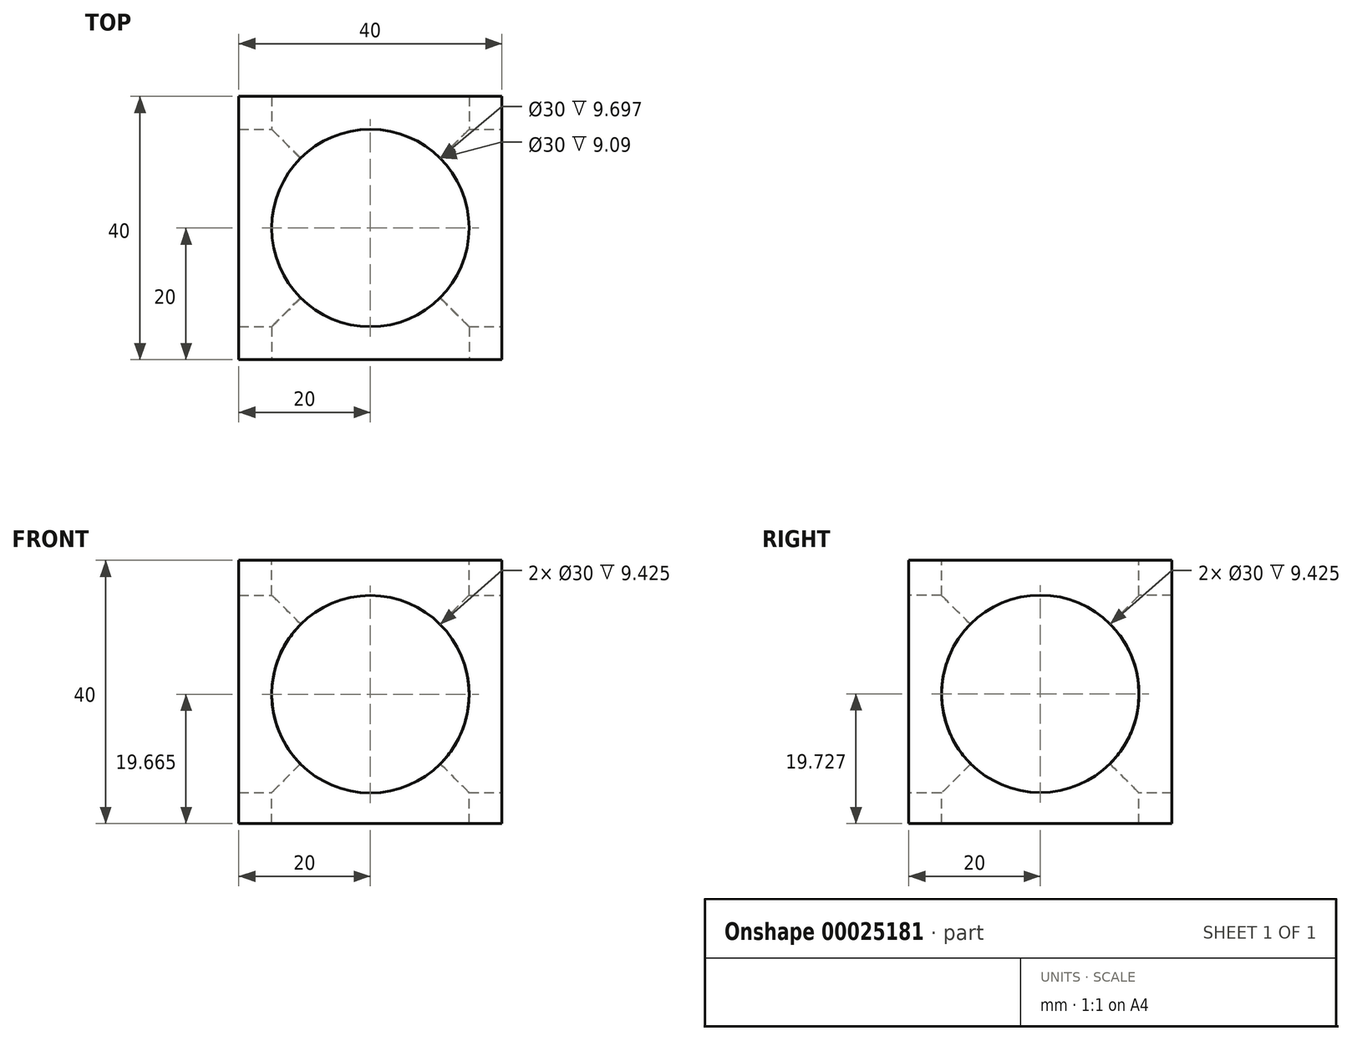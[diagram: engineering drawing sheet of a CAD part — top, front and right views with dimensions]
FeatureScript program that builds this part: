
annotation { "Feature Type Name" : "Feature", "Feature Type Description" : "" }
export const myFeature = defineFeature(function(context is Context, id is Id, definition is map)
    precondition{}
    {
        {
            var Q0;
            Q0=qCreatedBy(makeId("Top.planeOp"),FACE);
            var sketch = newSketch(context, id + "F0", { "sketchPlane" : qUnion([Q0])});
            skLineSegment(sketch, "E0.rect.bottom", {"start": v(20, -20) * mm, "end": v(-20, -20) * mm});
            skLineSegment(sketch, "E0.rect.top", {"start": v(20, 20) * mm, "end": v(-20, 20) * mm});
            skLineSegment(sketch, "E0.rect.left", {"start": v(20, -20) * mm, "end": v(20, 20) * mm});
            skLineSegment(sketch, "E0.rect.right", {"start": v(-20, -20) * mm, "end": v(-20, 20) * mm});
            skPoint(sketch, "E0.rect.middle", {"position": v(0, 0) * mm});
            skSolve(sketch);
        }
        {
            var Q0;
            Q0=makeQuery(id+"F0.imprint","IMPRINT",FACE,{"disambiguationData":[TD([[makeQuery(id+"F0.imprint","IMPRINT",EDGE,{"derivedFrom":sQuery(id+"F0.wireOp",EDGE,"E0.rect.bottom")}),-1.0]])]});
            extrude(context, id + "F1", {"entities" : qUnion([Q0]), "depth" : 40 * mm});
        }
        {
            var Q0;
            Q0=makeQuery(id+"F1.opExtrude","CAP_FACE",FACE,{"disambiguationData":[OSD([sQuery(id+"F0.wireOp",EDGE,"E0.rect.bottom"),sQuery(id+"F0.wireOp",EDGE,"E0.rect.top"),sQuery(id+"F0.wireOp",EDGE,"E0.rect.left"),sQuery(id+"F0.wireOp",EDGE,"E0.rect.right")])],"isStart":false});
            var sketch = newSketch(context, id + "F2", { "sketchPlane" : qUnion([Q0])});
            skCircle(sketch, "E1", {"center": v(0, 0) * mm, "radius": 15 * mm});
            skSolve(sketch);
        }
        {
            var Q0;
            Q0=makeQuery(id+"F2.imprint","IMPRINT",FACE,{"disambiguationData":[TD([[makeQuery(id+"F2.imprint","IMPRINT",EDGE,{"derivedFrom":sQuery(id+"F2.wireOp",EDGE,"E1")}),1.0]])]});
            extrude(context, id + "F3", {"entities" : qUnion([Q0]), "operationType" : NewBodyOperationType.REMOVE, "oppositeDirection" : true, "depth" : 40 * mm});
        }
        {
            var Q0;
            Q0=makeQuery(id+"F1.opExtrude","SWEPT_FACE",FACE,{"disambiguationData":[OSD([sQuery(id+"F0.wireOp",EDGE,"E0.rect.left")])]});
            var sketch = newSketch(context, id + "F4", { "sketchPlane" : qUnion([Q0])});
            skCircle(sketch, "E2", {"center": v(0, 19.73) * mm, "radius": 15 * mm});
            skSolve(sketch);
        }
        {
            var Q0;
            Q0=makeQuery(id+"F4.imprint","IMPRINT",FACE,{"disambiguationData":[TD([[makeQuery(id+"F4.imprint","IMPRINT",EDGE,{"derivedFrom":sQuery(id+"F4.wireOp",EDGE,"E2")}),1.0]])]});
            extrude(context, id + "F5", {"entities" : qUnion([Q0]), "operationType" : NewBodyOperationType.REMOVE, "oppositeDirection" : true, "depth" : 40 * mm});
        }
        {
            var Q0;
            Q0=makeQuery(id+"F1.opExtrude","SWEPT_FACE",FACE,{"disambiguationData":[OSD([sQuery(id+"F0.wireOp",EDGE,"E0.rect.bottom")])]});
            var sketch = newSketch(context, id + "F6", { "sketchPlane" : qUnion([Q0])});
            skCircle(sketch, "E3", {"center": v(0, 19.66) * mm, "radius": 15 * mm});
            skSolve(sketch);
        }
        {
            var Q0;
            Q0=makeQuery(id+"F6.imprint","IMPRINT",FACE,{"disambiguationData":[TD([[makeQuery(id+"F6.imprint","IMPRINT",EDGE,{"derivedFrom":sQuery(id+"F6.wireOp",EDGE,"E3")}),1.0]])]});
            extrude(context, id + "F7", {"entities" : qUnion([Q0]), "operationType" : NewBodyOperationType.REMOVE, "oppositeDirection" : true, "depth" : 40 * mm});
        }
    });
